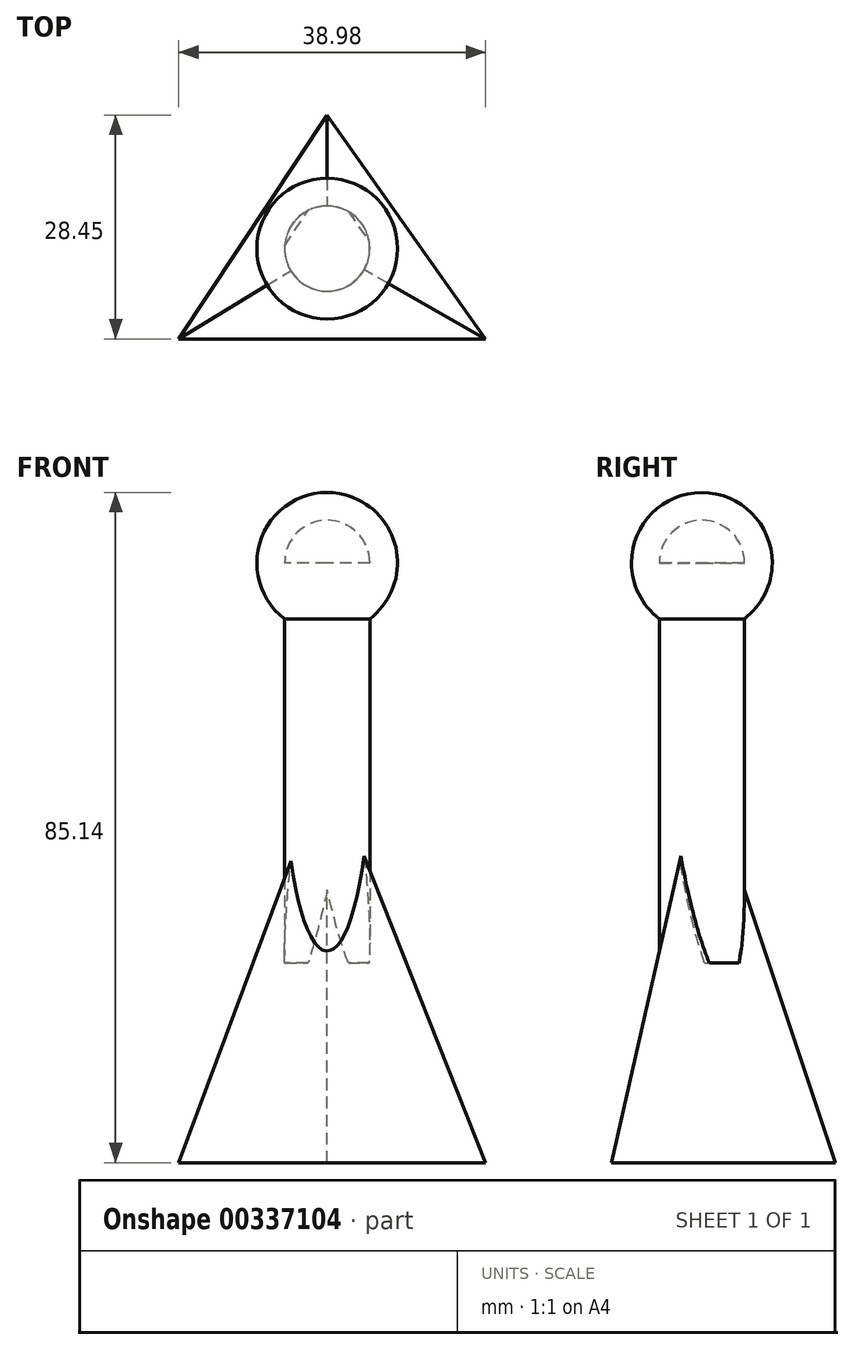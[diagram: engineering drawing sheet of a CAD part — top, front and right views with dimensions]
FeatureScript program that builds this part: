
annotation { "Feature Type Name" : "Feature", "Feature Type Description" : "" }
export const myFeature = defineFeature(function(context is Context, id is Id, definition is map)
    precondition{}
    {
        {
            var Q0;
            Q0=qCreatedBy(makeId("Top.planeOp"),FACE);
            var sketch = newSketch(context, id + "F0", { "sketchPlane" : qUnion([Q0])});
            skLineSegment(sketch, "E0", {"start": v(0, 28.45) * mm, "end": v(-18.86, 0) * mm});
            skLineSegment(sketch, "E1", {"start": v(-18.86, 0) * mm, "end": v(20.12, 0) * mm});
            skLineSegment(sketch, "E2", {"start": v(20.12, 0) * mm, "end": v(0, 28.45) * mm});
            skPoint(sketch, "E3.center.orphan", {"position": v(0, 11.47) * mm});
            skSolve(sketch);
        }
        {
            var Q0;
            Q0=qCreatedBy(makeId("Top.planeOp"),FACE);
            cPlane(context, id + "F1", {"entities" : qUnion([Q0]), "cplaneType" : CPlaneType.OFFSET, "offset" : 50.8 * mm, "width" : 152.4 * mm, "height" : 152.4 * mm});
        }
        {
            var Q0;
            Q0=qCreatedBy(id+"F1.planeOp",FACE);
            var sketch = newSketch(context, id + "F2", { "sketchPlane" : qUnion([Q0])});
            skCircle(sketch, "E4", {"center": v(0, 11.47) * mm, "radius": 5.4 * mm});
            skSolve(sketch);
        }
        {
            var Q0;
            Q0=makeQuery(id+"F0.imprint","IMPRINT",FACE,{"disambiguationData":[TD([[makeQuery(id+"F0.imprint","IMPRINT",EDGE,{"derivedFrom":sQuery(id+"F0.wireOp",EDGE,"E0")}),1.0]])]});
            var Q1;
            Q1=sQuery(id+"F2.wireOp",VERTEX,"E4.center");
            loft(context, id + "F3", {"sheetProfilesArray" : [{ "sheetProfileEntities" : qUnion([Q0]) }, { "sheetProfileEntities" : qUnion([Q1]) }]});
        }
        {
            var Q0;
            Q0=makeQuery(id+"F2.imprint","IMPRINT",FACE,{"disambiguationData":[TD([[makeQuery(id+"F2.imprint","IMPRINT",EDGE,{"derivedFrom":sQuery(id+"F2.wireOp",EDGE,"E4")}),1.0]])]});
            extrude(context, id + "F4", {"entities" : qUnion([Q0]), "operationType" : NewBodyOperationType.ADD, "depth" : 25.4 * mm, "hasSecondDirection" : true, "secondDirectionOppositeDirection" : true, "secondDirectionDepth" : 25.4 * mm});
        }
        {
            var Q0;
            Q0=makeQuery(id+"F4.opExtrude","CAP_FACE",FACE,{"disambiguationData":[OSD([sQuery(id+"F2.wireOp",EDGE,"E4")])],"isStart":false});
            var sketch = newSketch(context, id + "F5", { "sketchPlane" : qUnion([Q0])});
            skCircle(sketch, "E5", {"center": v(0, 11.47) * mm, "radius": 8.94 * mm});
            skLineSegment(sketch, "E6", {"start": v(0, 20.41) * mm, "end": v(0, 2.54) * mm});
            skSolve(sketch);
        }
        {
            var Q0;
            {var subQ0=sQuery(id+"F5.wireOp",EDGE,"E6");var subQ1=sQuery(id+"F5.wireOp",EDGE,"E5");var subQ2=makeQuery(id+"F5.imprint","INTERSECT",VERTEX,{"disambiguationData":[OD(0.0)],"derivedFrom":[subQ1,subQ0]});Q0=makeQuery(id+"F5.imprint","IMPRINT",FACE,{"disambiguationData":[TD([[makeQuery(id+"F5.imprint","IMPRINT",EDGE,{"disambiguationData":[TD([[subQ2,1.0]])],"derivedFrom":subQ1}),1.0]])]});}
            var Q1;
            Q1=sQuery(id+"F5.wireOp",EDGE,"E6");
            revolve(context, id + "F6", {"operationType" : NewBodyOperationType.ADD, "entities" : qUnion([Q0]), "axis" : qUnion([Q1]), "revolveType" : RevolveType.FULL});
        }
    });
